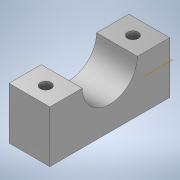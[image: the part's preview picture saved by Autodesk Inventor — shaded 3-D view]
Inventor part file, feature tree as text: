
AUTODESK INVENTOR PART (.ipt)
format: ipt  version: 2020 (Build 240168000, 168)  size: 125,440 bytes
history: native  units: mm
features: extrude x3, sketch x3, other x2
ambient origin geometry x8: Origin, YZ Plane, XZ Plane, XY Plane, X Axis, Y Axis, Z Axis, Center Point
bodies: Body1 (feature_tree)
feature tree (8):
  other  "Твердое тело1"
  extrude  "Выдавливание1"  Depth=15.0mm
  extrude  "Выдавливание2"  Depth=44.0mm
  other  "РабПлоскость1"
  extrude  "Выдавливание3"  Depth=16.0mm
  sketch  "Эскиз1"
  sketch  "Эскиз2"
  sketch  "Эскиз3"
